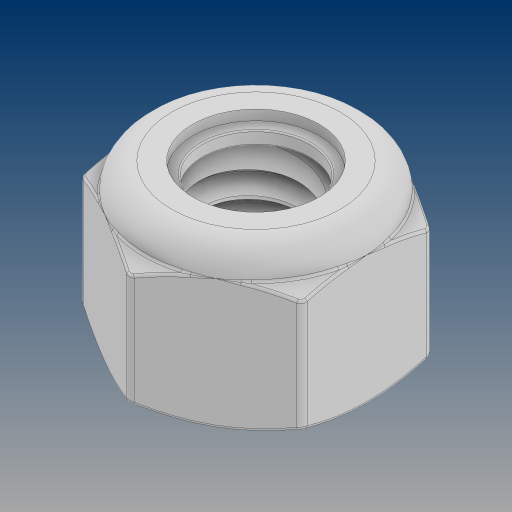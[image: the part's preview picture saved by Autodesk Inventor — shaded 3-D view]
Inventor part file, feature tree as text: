
AUTODESK INVENTOR PART (.ipt)
format: ipt  version: 2024.3 (Build 283343000, 343)  size: 598,016 bytes
history: native  units: in
note: dims shown in document units (in); Inventor stores cm internally (conversion verified against a paired STEP export)
features: fillet x1, boolean_combine x1
ambient origin geometry x8: Origin, YZ Plane, XZ Plane, XY Plane, X Axis, Y Axis, Z Axis, Center Point
bodies: Solid1 (feature_tree), Solid2 (feature_tree)
feature tree (2):
  fillet  "Fillet1"  [1 undecoded]
  boolean_combine  "Combine1"
note: 1 required parameter value undecoded (feature->parameter linkage not recoverable at this tier; creation-order binding heuristic only, values carry confidence <= 0.55)
